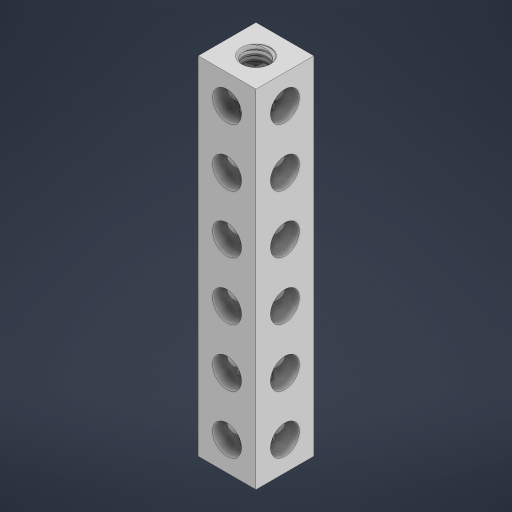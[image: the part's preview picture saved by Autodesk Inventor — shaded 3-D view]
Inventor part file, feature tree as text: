
AUTODESK INVENTOR PART (.ipt)
format: ipt  version: 2023 (Build 270158000, 158)  size: 1,358,336 bytes
history: native  units: in
note: dims shown in document units (in); Inventor stores cm internally (conversion verified against a paired STEP export)
features: mirror x1
ambient origin geometry x8: Origin, YZ Plane, XZ Plane, XY Plane, X Axis, Y Axis, Z Axis, Center Point
bodies: Solid1 (feature_tree)
feature tree (1):
  mirror  "Mirror3"
